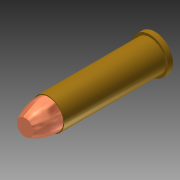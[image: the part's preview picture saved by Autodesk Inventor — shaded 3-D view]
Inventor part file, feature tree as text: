
AUTODESK INVENTOR PART (.ipt)
format: ipt  version: 2012 (Build 160160000, 160)  size: 142,848 bytes
history: native  units: in
note: dims shown in document units (in); Inventor stores cm internally (conversion verified against a paired STEP export)
features: sketch x9, extrude x7, plane x2, revolve x1, fillet x1
ambient origin geometry x8: Origin, YZ Plane, XZ Plane, XY Plane, X Axis, Y Axis, Z Axis, Center Point
bodies: Solid1 (feature_tree)
feature tree (20):
  extrude  "Extrusion1"  Depth=0.06in TaperAngle=0.0deg
  extrude  "Extrusion2"  Depth=1.23in TaperAngle=0.0deg
  extrude  "Extrusion3"  Depth=0.25in TaperAngle=0.0deg
  extrude  "Extrusion4"  Depth=0.29in TaperAngle=0.0deg
  extrude  "Extrusion5"  Depth=0.358in
  sketch  "Sketch6"  dims[d18=0.3in d19=0.2in]
  plane  "Work Plane2"
  revolve  "Revolution1"  [1 undecoded]
  extrude  "Extrusion8"  TaperAngle=360.0deg  [1 undecoded]
  fillet  "Fillet2"  Radius=0.44in
  extrude  "Extrusion9"  Depth=0.2in
  sketch  "Sketch1"  dims[d0=0.44in d1=0.06in d2=0.0in]
  sketch  "Sketch2"  dims[d6=0.379in d7=1.23in d8=0.0in]
  sketch  "Sketch3"  dims[d9=0.358in d10=0.25in d11=0.0in]
  sketch  "Sketch4"  dims[d12=0.04in d13=0.0in d14=0.29in d15=0.0in]
  sketch  "Sketch5"  dims[d16=1.54in d17=0.358in]
  plane  "Work Plane1"
  sketch  "Sketch7"  dims[d20=0.015in d21=360.0deg d34=0.44in]
  sketch  "Sketch10"  dims[d35=0.175in d36=0.2in]
  sketch  "Sketch11"  dims[d37=0.1in d38=0.0in d39=0.015in d40=0.1in d41=0.0in]
note: 2 required parameter values undecoded (feature->parameter linkage not recoverable at this tier; creation-order binding heuristic only, values carry confidence <= 0.55)